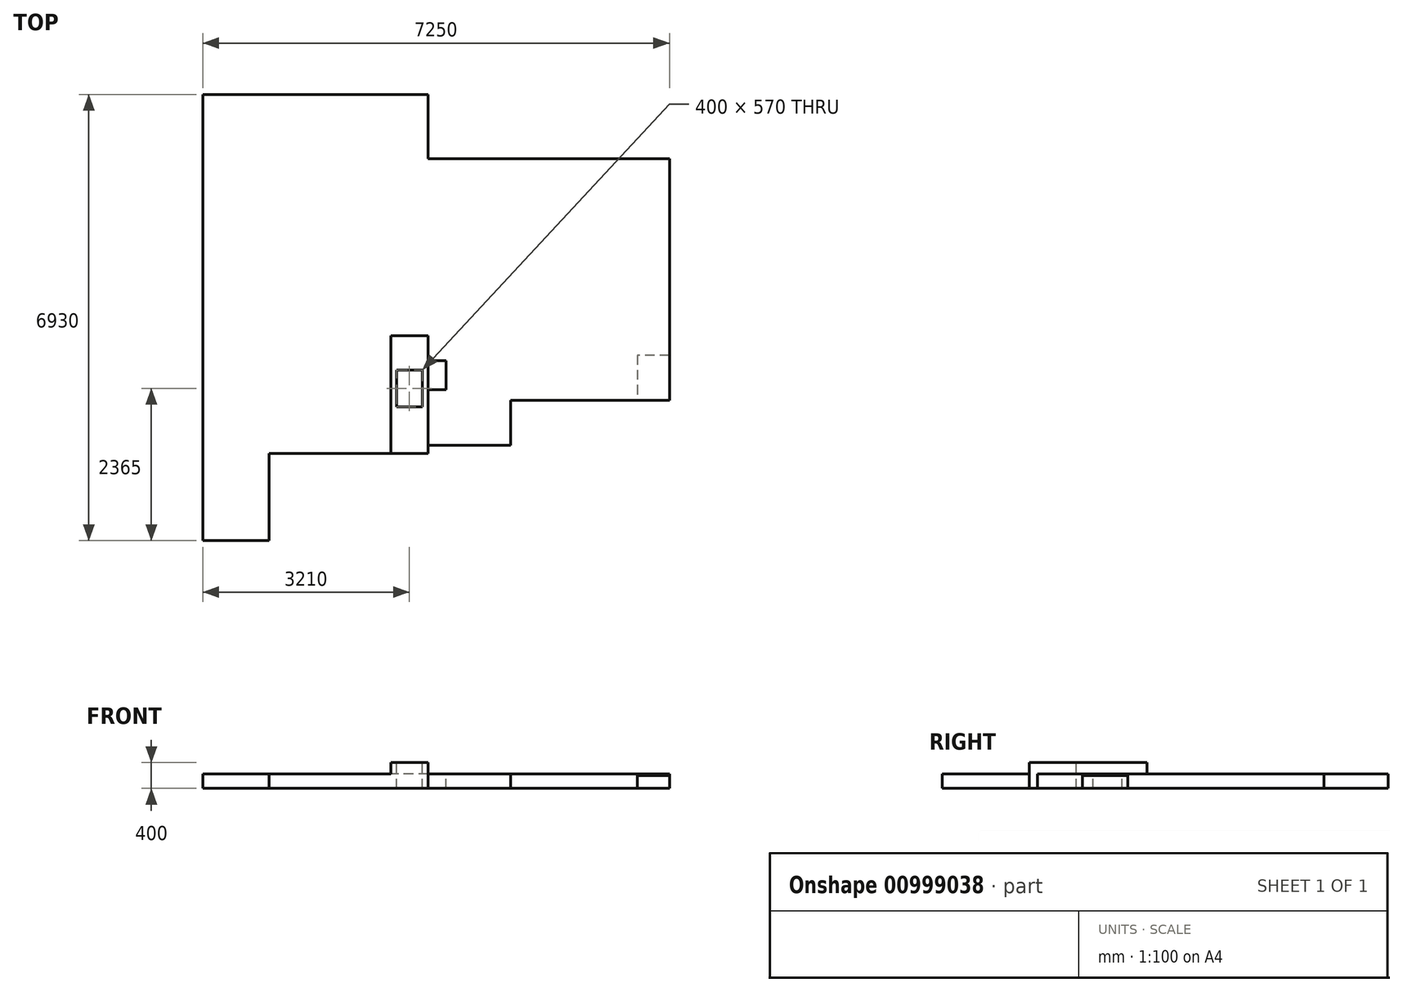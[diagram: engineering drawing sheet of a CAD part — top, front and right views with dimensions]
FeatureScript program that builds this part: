
annotation { "Feature Type Name" : "Feature", "Feature Type Description" : "" }
export const myFeature = defineFeature(function(context is Context, id is Id, definition is map)
    precondition{}
    {
        {
            var Q0;
            Q0=qCreatedBy(makeId("Top.planeOp"),FACE);
            var sketch = newSketch(context, id + "F0", { "sketchPlane" : qUnion([Q0])});
            skLineSegment(sketch, "E0", {"start": v(-4928.3, -4035.6) * mm, "end": v(-4928.3, -2685.6) * mm});
            skLineSegment(sketch, "E1", {"start": v(-4928.3, -2685.6) * mm, "end": v(-4928.3, 444.4) * mm});
            skLineSegment(sketch, "E2", {"start": v(-4928.3, 444.4) * mm, "end": v(-4928.3, 2894.4) * mm});
            skLineSegment(sketch, "E3", {"start": v(-1428.3, 1894.4) * mm, "end": v(-468.3, 1894.4) * mm});
            skLineSegment(sketch, "E4", {"start": v(-468.3, 1894.4) * mm, "end": v(791.7, 1894.4) * mm});
            skLineSegment(sketch, "E5", {"start": v(791.7, 1894.4) * mm, "end": v(2321.7, 1894.4) * mm});
            skLineSegment(sketch, "E6", {"start": v(2321.7, 1894.4) * mm, "end": v(2321.7, 1014.4) * mm});
            skLineSegment(sketch, "E7", {"start": v(2321.7, 1014.4) * mm, "end": v(2321.7, -235.6) * mm});
            skLineSegment(sketch, "E8", {"start": v(2321.7, -235.6) * mm, "end": v(2321.7, -1155.6) * mm});
            skLineSegment(sketch, "E9", {"start": v(2321.7, -1155.6) * mm, "end": v(2321.7, -1855.6) * mm});
            skLineSegment(sketch, "E10", {"start": v(2321.7, -1855.6) * mm, "end": v(-148.3, -1855.6) * mm});
            skLineSegment(sketch, "E11", {"start": v(-148.3, -1855.6) * mm, "end": v(-148.3, -2555.6) * mm});
            skLineSegment(sketch, "E12", {"start": v(-148.3, -2555.6) * mm, "end": v(-1428.3, -2555.6) * mm});
            skLineSegment(sketch, "E13", {"start": v(-1428.3, -2555.6) * mm, "end": v(-1428.3, -1155.6) * mm});
            skLineSegment(sketch, "E14", {"start": v(-1428.3, -1155.6) * mm, "end": v(-978.3, -1155.6) * mm});
            skLineSegment(sketch, "E15", {"start": v(2321.7, -1155.6) * mm, "end": v(-128.3, -1155.6) * mm});
            skLineSegment(sketch, "E16", {"start": v(-1428.3, -1155.6) * mm, "end": v(-1428.3, 954.4) * mm});
            skLineSegment(sketch, "E17", {"start": v(-4928.3, 444.4) * mm, "end": v(-1428.3, 444.4) * mm, "construction": true});
            skLineSegment(sketch, "E18", {"start": v(-4928.3, -4035.6) * mm, "end": v(-3898.3, -4035.6) * mm});
            skLineSegment(sketch, "E19", {"start": v(-3898.3, -4035.6) * mm, "end": v(-3898.3, -2685.6) * mm});
            skLineSegment(sketch, "E20", {"start": v(-3898.3, -2685.6) * mm, "end": v(-1428.3, -2685.6) * mm});
            skLineSegment(sketch, "E21", {"start": v(-1428.3, -2685.6) * mm, "end": v(-1428.3, -2555.6) * mm});
            skLineSegment(sketch, "E22", {"start": v(-1428.3, 1894.4) * mm, "end": v(-1428.3, 2894.4) * mm});
            skLineSegment(sketch, "E23", {"start": v(-1428.3, 2894.4) * mm, "end": v(-4928.3, 2894.4) * mm});
            skLineSegment(sketch, "E24", {"start": v(-2008.3, -2685.6) * mm, "end": v(-2008.3, -855.6) * mm});
            skLineSegment(sketch, "E25", {"start": v(-2008.3, -855.6) * mm, "end": v(-1428.3, -855.6) * mm});
            skLineSegment(sketch, "E26", {"start": v(-1428.3, -1775.6) * mm, "end": v(-488.3, -1775.6) * mm});
            skLineSegment(sketch, "E27", {"start": v(-488.3, -1775.6) * mm, "end": v(-488.3, -2555.6) * mm});
            skLineSegment(sketch, "E28", {"start": v(1821.7, -1155.6) * mm, "end": v(1821.7, -1855.6) * mm});
            skLineSegment(sketch, "E29.bottom", {"start": v(-1428.3, -1240.6) * mm, "end": v(-1148.3, -1240.6) * mm});
            skLineSegment(sketch, "E29.top", {"start": v(-1428.3, -1690.6) * mm, "end": v(-1148.3, -1690.6) * mm});
            skLineSegment(sketch, "E29.left", {"start": v(-1428.3, -1240.6) * mm, "end": v(-1428.3, -1690.6) * mm});
            skLineSegment(sketch, "E29.right", {"start": v(-1148.3, -1240.6) * mm, "end": v(-1148.3, -1690.6) * mm});
            skLineSegment(sketch, "E30.bottom", {"start": v(-1918.3, -1385.6) * mm, "end": v(-1518.3, -1385.6) * mm});
            skLineSegment(sketch, "E30.top", {"start": v(-1918.3, -1955.6) * mm, "end": v(-1518.3, -1955.6) * mm});
            skLineSegment(sketch, "E30.left", {"start": v(-1918.3, -1385.6) * mm, "end": v(-1918.3, -1955.6) * mm});
            skLineSegment(sketch, "E30.right", {"start": v(-1518.3, -1385.6) * mm, "end": v(-1518.3, -1955.6) * mm});
            skSolve(sketch);
        }
        {
            var Q0;
            Q0=makeQuery(id+"F0.imprint","IMPRINT",FACE,{"disambiguationData":[TD([[makeQuery(id+"F0.imprint","IMPRINT",EDGE,{"derivedFrom":sQuery(id+"F0.wireOp",EDGE,"E0")}),-1.0]])]});
            var Q1;
            {var subQ0=sQuery(id+"F0.wireOp",EDGE,"E21");Q1=makeQuery(id+"F0.imprint","IMPRINT",FACE,{"disambiguationData":[TD([[makeQuery(id+"F0.imprint","IMPRINT",EDGE,{"derivedFrom":subQ0}),1.0]])]});}
            var Q2;
            {var subQ4=sQuery(id+"F0.wireOp",EDGE,"E26");Q2=makeQuery(id+"F0.imprint","IMPRINT",FACE,{"disambiguationData":[TD([[makeQuery(id+"F0.imprint","IMPRINT",EDGE,{"derivedFrom":subQ4}),-1.0]])]});}
            var Q3;
            Q3=sQuery(id+"F0.wireOp",EDGE,"E1");
            var Q4;
            Q4=sQuery(id+"F0.wireOp",EDGE,"E0");
            var Q5;
            Q5=sQuery(id+"F0.wireOp",EDGE,"E18");
            var Q6;
            Q6=sQuery(id+"F0.wireOp",EDGE,"E19");
            var Q7;
            Q7=sQuery(id+"F0.wireOp",EDGE,"E20");
            var Q8;
            Q8=sQuery(id+"F0.wireOp",EDGE,"E24");
            var Q9;
            Q9=sQuery(id+"F0.wireOp",EDGE,"E30.top");
            var Q10;
            Q10=sQuery(id+"F0.wireOp",EDGE,"E30.left");
            var Q11;
            Q11=sQuery(id+"F0.wireOp",EDGE,"E30.right");
            var Q12;
            Q12=sQuery(id+"F0.wireOp",EDGE,"E30.bottom");
            var Q13;
            Q13=sQuery(id+"F0.wireOp",EDGE,"E12");
            var Q14;
            Q14=sQuery(id+"F0.wireOp",EDGE,"E13");
            var Q15;
            Q15=sQuery(id+"F0.wireOp",EDGE,"E21");
            var Q16;
            Q16=sQuery(id+"F0.wireOp",EDGE,"E16");
            var Q17;
            Q17=sQuery(id+"F0.wireOp",EDGE,"E25");
            var Q18;
            Q18=sQuery(id+"F0.wireOp",EDGE,"E28");
            var Q19;
            Q19=sQuery(id+"F0.wireOp",EDGE,"E27");
            var Q20;
            Q20=sQuery(id+"F0.wireOp",EDGE,"E26");
            var Q21;
            Q21=sQuery(id+"F0.wireOp",EDGE,"E23");
            var Q22;
            Q22=sQuery(id+"F0.wireOp",EDGE,"E3");
            var Q23;
            Q23=sQuery(id+"F0.wireOp",EDGE,"E22");
            var Q24;
            Q24=sQuery(id+"F0.wireOp",EDGE,"E4");
            var Q25;
            Q25=sQuery(id+"F0.wireOp",EDGE,"E5");
            var Q26;
            Q26=sQuery(id+"F0.wireOp",EDGE,"E29.top");
            var Q27;
            Q27=sQuery(id+"F0.wireOp",EDGE,"E6");
            var Q28;
            Q28=sQuery(id+"F0.wireOp",EDGE,"E29.bottom");
            var Q29;
            Q29=sQuery(id+"F0.wireOp",EDGE,"E7");
            var Q30;
            Q30=sQuery(id+"F0.wireOp",EDGE,"E8");
            var Q31;
            Q31=sQuery(id+"F0.wireOp",EDGE,"E15");
            var Q32;
            Q32=sQuery(id+"F0.wireOp",EDGE,"E9");
            var Q33;
            Q33=sQuery(id+"F0.wireOp",EDGE,"E10");
            var Q34;
            Q34=sQuery(id+"F0.wireOp",EDGE,"E29.right");
            var Q35;
            Q35=sQuery(id+"F0.wireOp",EDGE,"E14");
            var Q36;
            Q36=sQuery(id+"F0.wireOp",EDGE,"E11");
            var Q37;
            Q37=sQuery(id+"F0.wireOp",EDGE,"E29.left");
            var Q38;
            Q38=sQuery(id+"F0.wireOp",EDGE,"E2");
            extrude(context, id + "F1", {"entities" : qUnion([Q0, Q1, Q2]), "surfaceEntities" : qUnion([Q3, Q4, Q5, Q6, Q7, Q8, Q9, Q10, Q11, Q12, Q13, Q14, Q15, Q16, Q17, Q18, Q19, Q20, Q21, Q22, Q23, Q24, Q25, Q26, Q27, Q28, Q29, Q30, Q31, Q32, Q33, Q34, Q35, Q36, Q37, Q38]), "oppositeDirection" : true, "depth" : 200 * mm, "offsetDistance" : 25 * mm});
        }
        {
            var Q0;
            Q0 = qSketchRegion(id + "F0", true);
            extrude(context, id + "F2", {"entities" : qUnion([Q0]), "operationType" : NewBodyOperationType.ADD, "depth" : 25 * mm, "offsetDistance" : 25 * mm});
        }
        {
            var Q0;
            {var subQ0=sQuery(id+"F0.wireOp",EDGE,"E21");Q0=makeQuery(id+"F0.imprint","IMPRINT",FACE,{"disambiguationData":[TD([[makeQuery(id+"F0.imprint","IMPRINT",EDGE,{"derivedFrom":subQ0}),1.0]])]});}
            extrude(context, id + "F3", {"entities" : qUnion([Q0]), "operationType" : NewBodyOperationType.ADD, "depth" : 200 * mm, "offsetDistance" : 25 * mm});
        }
    });
